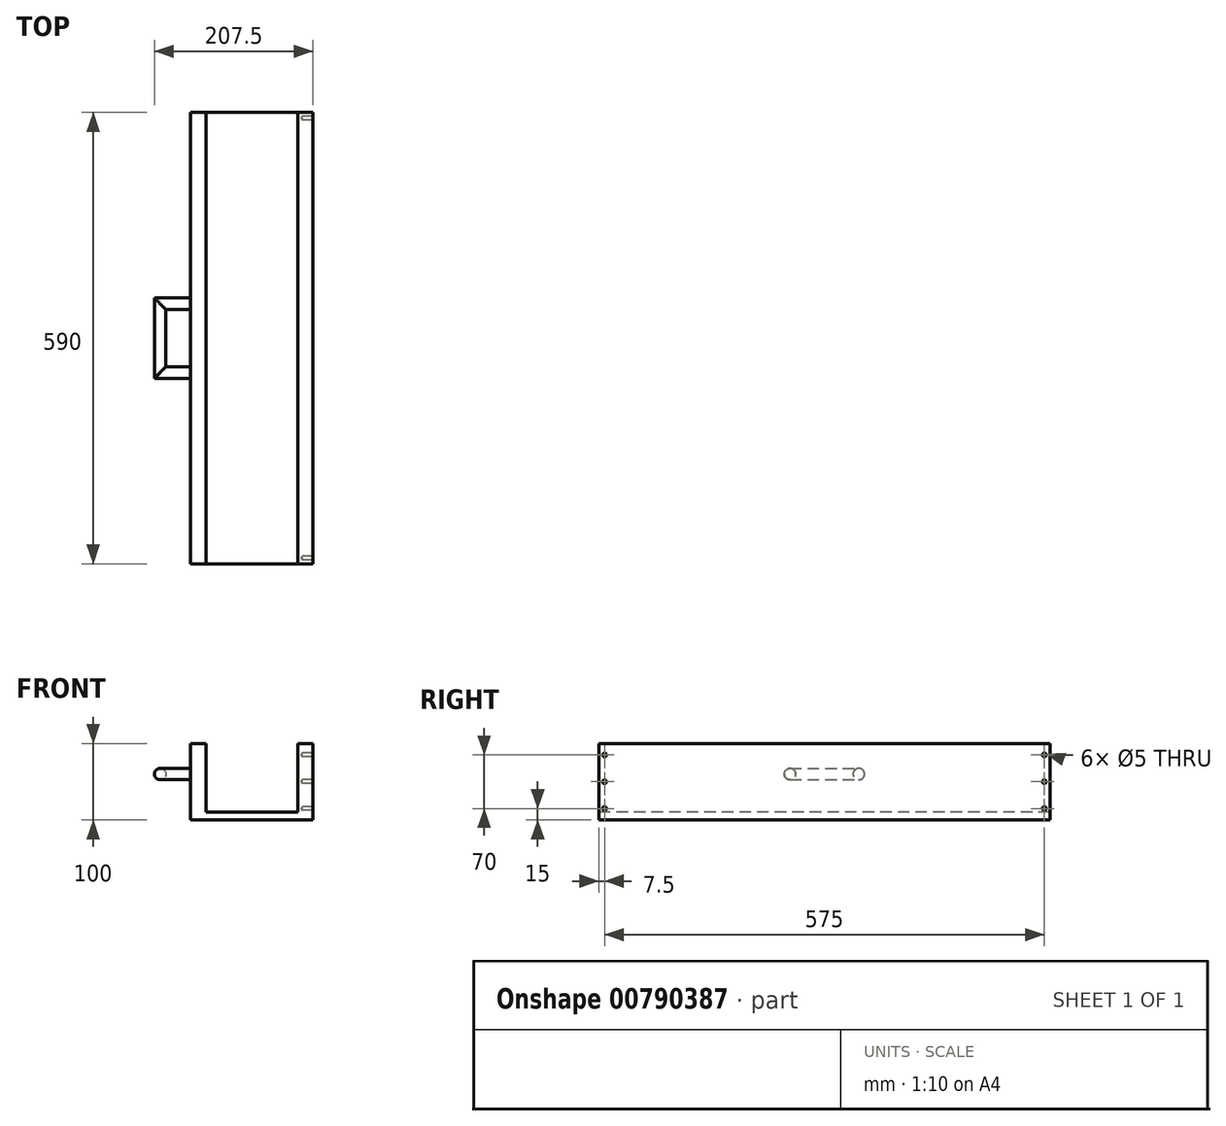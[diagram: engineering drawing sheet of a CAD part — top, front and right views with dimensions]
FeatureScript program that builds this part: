
annotation { "Feature Type Name" : "Feature", "Feature Type Description" : "" }
export const myFeature = defineFeature(function(context is Context, id is Id, definition is map)
    precondition{}
    {
        {
            var Q0;
            Q0=qCreatedBy(makeId("Front.planeOp"),FACE);
            var sketch = newSketch(context, id + "F0", { "sketchPlane" : qUnion([Q0])});
            skLineSegment(sketch, "E0.top", {"start": v(80, 90) * mm, "end": v(60, 90) * mm});
            skLineSegment(sketch, "E0.left", {"start": v(80, -10) * mm, "end": v(80, 90) * mm});
            skLineSegment(sketch, "E0.right", {"start": v(-80, -10) * mm, "end": v(-80, 90) * mm});
            skPoint(sketch, "E0.middle", {"position": v(0, 0) * mm});
            skLineSegment(sketch, "E1.trimOffspring", {"start": v(-60, 90) * mm, "end": v(-80, 90) * mm});
            skLineSegment(sketch, "E2", {"start": v(-80, -10) * mm, "end": v(80, -10) * mm});
            skPoint(sketch, "E3", {"position": v(-70, 75) * mm});
            skPoint(sketch, "E4", {"position": v(70, 75) * mm});
            skPoint(sketch, "E5", {"position": v(70, 40) * mm});
            skPoint(sketch, "E6", {"position": v(-70, 40) * mm});
            skPoint(sketch, "E7", {"position": v(-70, 5) * mm});
            skPoint(sketch, "E8", {"position": v(70, 5) * mm});
            skPoint(sketch, "E9", {"position": v(0, 5) * mm});
            skPoint(sketch, "E10", {"position": v(-70, 90) * mm});
            skPoint(sketch, "E11", {"position": v(70, 90) * mm});
            skLineSegment(sketch, "E12", {"start": v(0, 0) * mm, "end": v(60, 0) * mm});
            skLineSegment(sketch, "E13", {"start": v(60, 90) * mm, "end": v(60, 0) * mm});
            skLineSegment(sketch, "E14", {"start": v(0, 0) * mm, "end": v(-60, 0) * mm});
            skLineSegment(sketch, "E15", {"start": v(-60, 90) * mm, "end": v(-60, 0) * mm});
            skPoint(sketch, "E16.center.orphan", {"position": v(0, 90) * mm});
            skSolve(sketch);
        }
        {
            var Q0;
            Q0=qSketchRegion(id+"F0",true);
            extrude(context, id + "F1", {"entities" : qUnion([Q0]), "oppositeDirection" : true, "depth" : 590 * mm, "offsetDistance" : 25 * mm});
        }
        {
            var Q0;
            Q0=makeQuery(id+"F1.opExtrude","SWEPT_FACE",FACE,{"disambiguationData":[OSD([sQuery(id+"F0.wireOp",EDGE,"E0.right")])]});
            var sketch = newSketch(context, id + "F2", { "sketchPlane" : qUnion([Q0])});
            skCircle(sketch, "E17", {"center": v(-250, 50) * mm, "radius": 7.5 * mm});
            skCircle(sketch, "E18", {"center": v(-340, 50) * mm, "radius": 7.5 * mm});
            skSolve(sketch);
        }
        {
            var Q0;
            Q0=makeQuery(id+"F1.opExtrude","SWEPT_FACE",FACE,{"disambiguationData":[OSD([sQuery(id+"F0.wireOp",EDGE,"E2")])]});
            cPlane(context, id + "F3", {"entities" : qUnion([Q0]), "cplaneType" : CPlaneType.OFFSET, "offset" : 100 * mm, "oppositeDirection" : true, "width" : 150 * mm, "height" : 150 * mm});
        }
        {
            var Q0;
            Q0=qCreatedBy(id+"F3.planeOp",FACE);
            var sketch = newSketch(context, id + "F4", { "sketchPlane" : qUnion([Q0])});
            skLineSegment(sketch, "E19", {"start": v(-80, -250) * mm, "end": v(-120, -250) * mm});
            skLineSegment(sketch, "E20", {"start": v(-120, -250) * mm, "end": v(-120, -340) * mm});
            skLineSegment(sketch, "E21", {"start": v(-120, -340) * mm, "end": v(-80, -340) * mm});
            skSolve(sketch);
        }
        {
            var Q0;
            Q0=makeQuery(id+"F2.imprint","IMPRINT",FACE,{"disambiguationData":[TD([[makeQuery(id+"F2.imprint","IMPRINT",EDGE,{"derivedFrom":sQuery(id+"F2.wireOp",EDGE,"E17")}),1.0]])]});
            var Q1;
            Q1=sQuery(id+"F4.wireOp",EDGE,"E19");
            var Q2;
            Q2=sQuery(id+"F4.wireOp",EDGE,"E20");
            var Q3;
            Q3=sQuery(id+"F4.wireOp",EDGE,"E21");
            sweep(context, id + "F5", {"operationType" : NewBodyOperationType.ADD, "profiles" : qUnion([Q0]), "path" : qUnion([Q1, Q2, Q3])});
        }
        {
            var Q0;
            Q0=makeQuery(id+"F1.opExtrude","SWEPT_FACE",FACE,{"disambiguationData":[OSD([sQuery(id+"F0.wireOp",EDGE,"E0.left")])]});
            var sketch = newSketch(context, id + "F6", { "sketchPlane" : qUnion([Q0])});
            skPoint(sketch, "E22", {"position": v(582.5, 5) * mm});
            skPoint(sketch, "E23", {"position": v(582.5, 40) * mm});
            skPoint(sketch, "E24", {"position": v(582.5, 75) * mm});
            skPoint(sketch, "E25", {"position": v(295, -10) * mm});
            skLineSegment(sketch, "E26", {"start": v(295, -52.55) * mm, "end": v(295, 96.65) * mm, "construction": true});
            skPoint(sketch, "E27.MirrorP", {"position": v(7.5, 5) * mm});
            skPoint(sketch, "E28.MirrorP", {"position": v(7.5, 40) * mm});
            skPoint(sketch, "E29.MirrorP", {"position": v(7.5, 75) * mm});
            skSolve(sketch);
        }
        {
            var Q0;
            Q0=sQuery(id+"F6.wireOp",VERTEX,"E22");
            var Q1;
            Q1=sQuery(id+"F6.wireOp",VERTEX,"E23");
            var Q2;
            Q2=sQuery(id+"F6.wireOp",VERTEX,"E24");
            var Q3;
            Q3=sQuery(id+"F6.wireOp",VERTEX,"E27.MirrorP");
            var Q4;
            Q4=sQuery(id+"F6.wireOp",VERTEX,"E28.MirrorP");
            var Q5;
            Q5=sQuery(id+"F6.wireOp",VERTEX,"E29.MirrorP");
            var Q6;
            Q6=makeQuery(id+"F1.opExtrude","SWEPT_BODY",BODY,{"disambiguationData":[OSD([sQuery(id+"F0.wireOp",EDGE,"E0.top"),sQuery(id+"F0.wireOp",EDGE,"E0.left"),sQuery(id+"F0.wireOp",EDGE,"E0.right"),sQuery(id+"F0.wireOp",EDGE,"E1.trimOffspring"),sQuery(id+"F0.wireOp",EDGE,"E2"),sQuery(id+"F0.wireOp",EDGE,"E12"),sQuery(id+"F0.wireOp",EDGE,"E13"),sQuery(id+"F0.wireOp",EDGE,"E14"),sQuery(id+"F0.wireOp",EDGE,"E15")])]});
            hole(context, id + "F7", {"style" : HoleStyle.SIMPLE, "endStyle" : HoleEndStyle.BLIND, "standardTappedOrClearance" : lookupTablePath({ "standard" : "ISO", "engagement" : "75%", "pitch" : "1 mm", "size" : "M6", "type" : "Tapped" }), "standardBlindInLast" : lookupTablePath({ "standard" : "ISO", "engagement" : "75%", "pitch" : "1 mm", "size" : "M6", "type" : "Tapped" }), "holeDiameter" : 5 * mm, "majorDiameter" : 6 * mm, "showTappedDepth" : true, "holeDepth" : 14.25 * mm, "isTappedThrough" : true, "tappedDepth" : 11.25 * mm, "tapClearance" : 3, "startFromSketch" : true, "locations" : qUnion([Q0, Q1, Q2, Q3, Q4, Q5]), "scope" : qUnion([Q6])});
        }
    });
